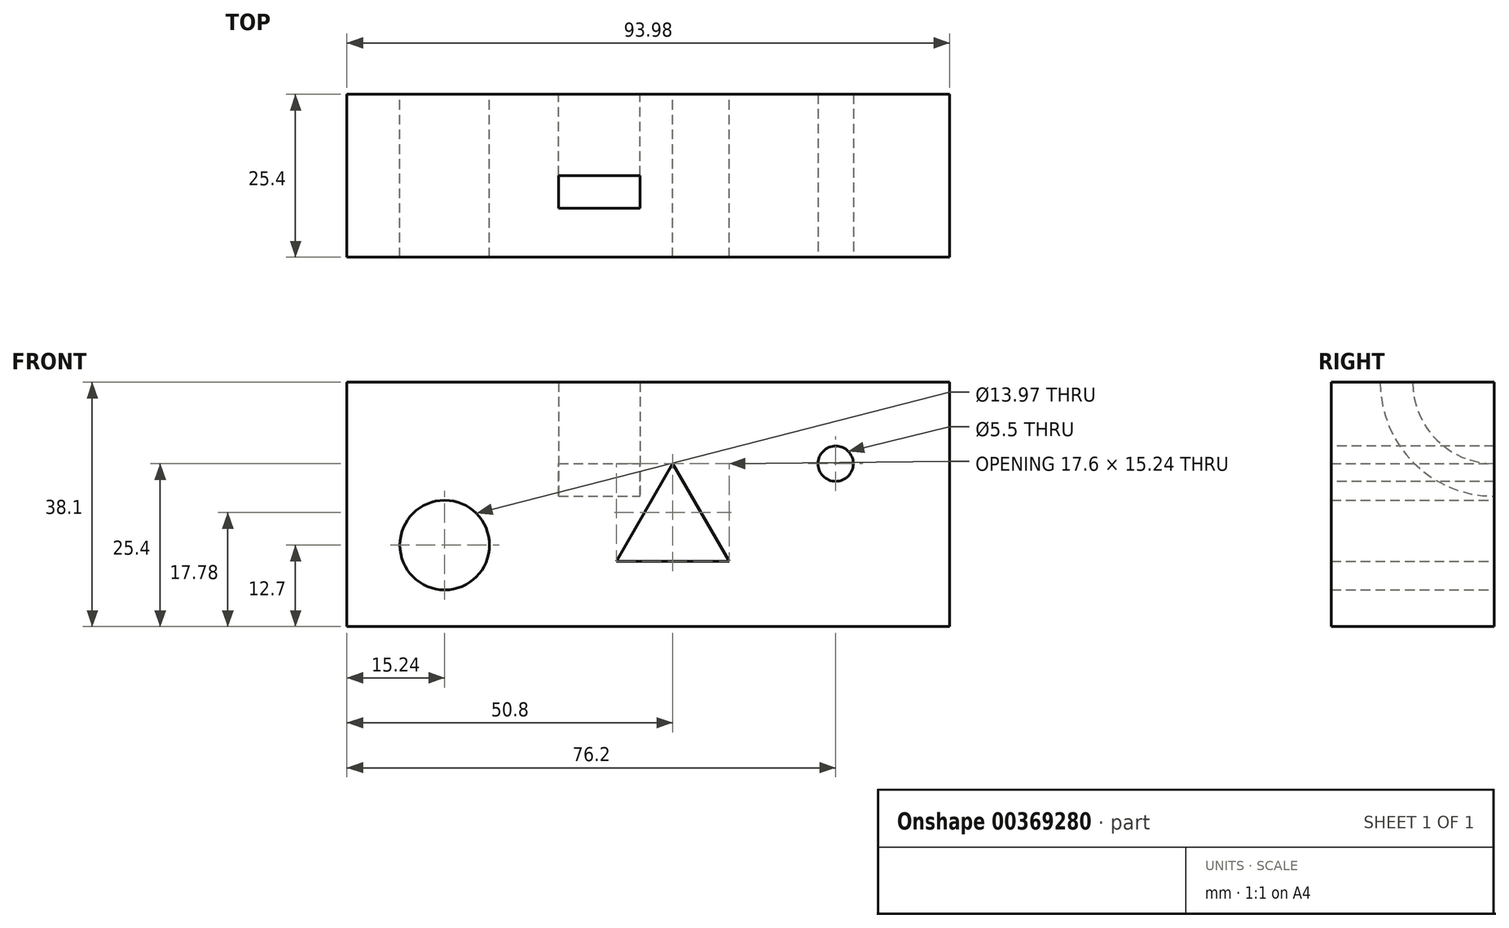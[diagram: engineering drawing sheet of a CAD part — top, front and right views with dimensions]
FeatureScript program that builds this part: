
annotation { "Feature Type Name" : "Feature", "Feature Type Description" : "" }
export const myFeature = defineFeature(function(context is Context, id is Id, definition is map)
    precondition{}
    {
        {
            var Q0;
            Q0=qCreatedBy(makeId("Front.planeOp"),FACE);
            var sketch = newSketch(context, id + "F0", { "sketchPlane" : qUnion([Q0])});
            skLineSegment(sketch, "E0.bottom", {"start": v(0, 0) * mm, "end": v(93.98, 0) * mm});
            skLineSegment(sketch, "E0.top", {"start": v(0, 38.1) * mm, "end": v(93.98, 38.1) * mm});
            skLineSegment(sketch, "E0.left", {"start": v(0, 0) * mm, "end": v(0, 38.1) * mm});
            skLineSegment(sketch, "E0.right", {"start": v(93.98, 0) * mm, "end": v(93.98, 38.1) * mm});
            skCircle(sketch, "E1", {"center": v(15.24, 12.7) * mm, "radius": 6.99 * mm});
            skCircle(sketch, "E2.cCircle", {"center": v(50.8, 15.24) * mm, "radius": 5.08 * mm, "construction": true});
            skLineSegment(sketch, "E2.0", {"start": v(50.8, 25.4) * mm, "end": v(59.6, 10.16) * mm});
            skLineSegment(sketch, "E2.1", {"start": v(59.6, 10.16) * mm, "end": v(42, 10.16) * mm});
            skLineSegment(sketch, "E2.2", {"start": v(42, 10.16) * mm, "end": v(50.8, 25.4) * mm});
            skPoint(sketch, "E2.0.midPoint", {"position": v(55.2, 17.78) * mm});
            skSolve(sketch);
        }
        {
            var Q0;
            Q0=makeQuery(id+"F0.imprint","IMPRINT",FACE,{"disambiguationData":[TD([[makeQuery(id+"F0.imprint","IMPRINT",EDGE,{"derivedFrom":sQuery(id+"F0.wireOp",EDGE,"E0.bottom")}),1.0]])]});
            extrude(context, id + "F1", {"entities" : qUnion([Q0]), "depth" : 25.4 * mm});
        }
        {
            var Q0;
            Q0=makeQuery(id+"F1.opExtrude","CAP_FACE",FACE,{"disambiguationData":[OSD([sQuery(id+"F0.wireOp",EDGE,"E0.bottom"),sQuery(id+"F0.wireOp",EDGE,"E0.top"),sQuery(id+"F0.wireOp",EDGE,"E0.left"),sQuery(id+"F0.wireOp",EDGE,"E0.right"),sQuery(id+"F0.wireOp",EDGE,"E1"),sQuery(id+"F0.wireOp",EDGE,"E2.0"),sQuery(id+"F0.wireOp",EDGE,"E2.1"),sQuery(id+"F0.wireOp",EDGE,"E2.2")])],"isStart":false});
            var sketch = newSketch(context, id + "F2", { "sketchPlane" : qUnion([Q0])});
            skPoint(sketch, "E3", {"position": v(76.2, 25.4) * mm});
            skSolve(sketch);
        }
        {
            var Q0;
            Q0=sQuery(id+"F2.wireOp",VERTEX,"E3");
            var Q1;
            Q1=makeQuery(id+"F1.opExtrude","SWEPT_BODY",BODY,{"disambiguationData":[OSD([sQuery(id+"F0.wireOp",EDGE,"E0.bottom"),sQuery(id+"F0.wireOp",EDGE,"E0.top"),sQuery(id+"F0.wireOp",EDGE,"E0.left"),sQuery(id+"F0.wireOp",EDGE,"E0.right"),sQuery(id+"F0.wireOp",EDGE,"E1"),sQuery(id+"F0.wireOp",EDGE,"E2.0"),sQuery(id+"F0.wireOp",EDGE,"E2.1"),sQuery(id+"F0.wireOp",EDGE,"E2.2")])]});
            hole(context, id + "F3", {"style" : HoleStyle.SIMPLE, "endStyle" : HoleEndStyle.THROUGH, "standardTappedOrClearance" : lookupTablePath({ "standard" : "ISO", "fit" : "Normal", "size" : "M5", "type" : "Clearance" }), "standardBlindInLast" : lookupTablePath({ "fit" : "Standard", "standard" : "ISO", "size" : "M5", "type" : "Clearance" }), "holeDiameter" : 5.5 * mm, "isTappedThrough" : true, "tappedDepth" : 12.7 * mm, "tapClearance" : 3, "locations" : qUnion([Q0]), "scope" : qUnion([Q1])});
        }
        {
            var Q0;
            Q0=makeQuery(id+"F1.opExtrude","SWEPT_FACE",FACE,{"disambiguationData":[OSD([sQuery(id+"F0.wireOp",EDGE,"E0.top")])]});
            var sketch = newSketch(context, id + "F4", { "sketchPlane" : qUnion([Q0])});
            skLineSegment(sketch, "E4.bottom", {"start": v(33.02, -12.7) * mm, "end": v(45.72, -12.7) * mm});
            skLineSegment(sketch, "E4.top", {"start": v(33.02, -17.78) * mm, "end": v(45.72, -17.78) * mm});
            skLineSegment(sketch, "E4.left", {"start": v(33.02, -12.7) * mm, "end": v(33.02, -17.78) * mm});
            skLineSegment(sketch, "E4.right", {"start": v(45.72, -12.7) * mm, "end": v(45.72, -17.78) * mm});
            skSolve(sketch);
        }
        {
            var Q0;
            Q0 = qSketchRegion(id + "F4", true);
            var Q1;
            Q1=makeQuery(id+"F1.opExtrude","CAP_EDGE",EDGE,{"disambiguationData":[OSD([sQuery(id+"F0.wireOp",EDGE,"E0.top")])],"isStart":true});
            revolve(context, id + "F5", {"operationType" : NewBodyOperationType.REMOVE, "entities" : qUnion([Q0]), "axis" : qUnion([Q1]), "revolveType" : RevolveType.FULL, "oppositeDirection" : true});
        }
    });
